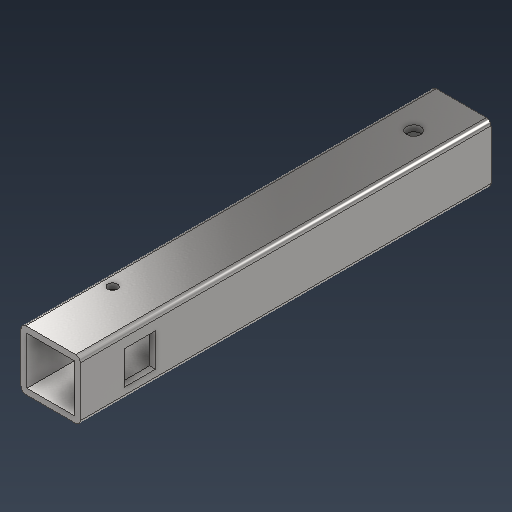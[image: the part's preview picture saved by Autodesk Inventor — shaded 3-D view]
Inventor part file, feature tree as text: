
AUTODESK INVENTOR PART (.ipt)
format: ipt  version: 2021 (Build 250183000, 183)  size: 237,568 bytes
history: native  units: mm
features: sketch x4, extrude x3, other x2, fillet x1, split x1, hole x1, plane x1
ambient origin geometry x8: Origin, YZ Plane, XZ Plane, XY Plane, X Axis, Y Axis, Z Axis, Center Point
bodies: Solid1 (feature_tree)
feature tree (13):
  extrude  "Extrusion1"  Depth=25.0mm
  fillet  "Fillet1"  Radius=12.5mm
  other  "endPlane"
  split  "Split1"
  other  "midPlane"
  sketch  "Sketch2"  dims[d3=12.5mm d4=2.5mm]
  extrude  "Extrusion2"  Depth=2.5mm
  hole  "Hole2"  [1 undecoded]
  plane  "Work Plane3"
  extrude  "Extrusion3"  Depth=14.0mm
  sketch  "Sketch1"  dims[d0=25.0mm d1=25.0mm d2=12.5mm]
  sketch  "Sketch3"  dims[d5=1000.0mm d6=0.0mm d7=2.0mm]
  sketch  "Sketch4"  dims[d8=-172.5mm d28=14.0mm d29=18.5mm d30=13.0mm d31=10.0mm d32=0.0mm d36=6.0mm d38=4.0mm d39=6.0mm d40=4.0mm d41=2.0mm d42=90.0deg d43=8.0mm d44=20.594885mm d45=1.0mm d46=6.0mm d47=0.0mm d48=20.0mm d49=0.0mm d50=0.0mm d51=0.0mm]
note: 1 required parameter value undecoded (feature->parameter linkage not recoverable at this tier; creation-order binding heuristic only, values carry confidence <= 0.55)
